# Revit family: EURS_63_LF_FB_Pacific LED_WT490C L700
name_source: partatom
category: Lighting Fixtures
units: mm (PartAtom-declared; Revit-internal decimal feet)

## family parameters
Cut with Voids When Loaded = No
Host = Face
Light Source = No
Part Type = Normal
Room Calculation Point = No
Round Connector Dimension = Use Diameter
Shared = Yes

## types (1)
- EURS_63_LF_FB_Pacific LED_WT490C L700
    Apparent Load = 15 VA
    BIM Library - URL = http://www.lighting.philips.com
    Content modified date = 23-11-2021
    Content version = 1.0
    Default Elevation = 0 mm  [stored 0 ft]
    Description = PacificLED Gen5
    EOC = EOC CODE
    Hanger = 30 mm  [stored 0.0984252 ft]
    Hanger distance = 420 mm  [stored 1.37795 ft]
    Lamp = LAMP TYPE
    Lamp type = WT490C IES Data : PSD EL3 L700 1 xLED23S_830 NB-HRO
    Last IES update = 23-11-2021
    Length = 660 mm  [stored 2.16535 ft]
    Light source = 82 mm
    Manufacturer = Philips
    Model = WT490C L700
    Product catalog - URL = http://www.lighting.philips.com
    Side = 30 mm  [stored 0.0984252 ft]
    Type Comments = Face Based
    URL = http://www.lighting.philips.com
    Width = 96 mm  [stored 0.314961 ft]

note: [stored X ft] marks values corroborated as IEEE doubles in the binary element streams (Revit-internal decimal feet)

## geometry (parser evidence)
native form markers: Sweep x11
no freeform markers — native parametric forms only
